# Revit family: Gira_291803
name_source: partatom
category: Electrical Fixtures
revit_build: Autodesk Revit 2017 (Build: 20160225_1515(x64)
units: mm (PartAtom-declared; Revit-internal decimal feet)

## family parameters
Cut with Voids When Loaded = No
Host = Face
Maintain Annotation Orientation = Yes
Part Type = Normal
Room Calculation Point = No
Round Connector Dimension = Use Diameter
Shared = No

## types (1)
- UPS emergency set System 55 p.white
    Assembly arrangement = Basic element
    Available = No
    BIM (1) = https://media.stage.bim.site und Tasten.rfa?public/gira/36a6b08/Sys55_Komplettgerät_Schalten und Tasten.rfa
    Category = System device clinic-installation
    Data sheet (1) = https://katalog.gira.de
    Default Elevation = 1219 mm
    Description = UPS emerg.set Sys55 PW,UPS for the emergency set,,pure white glossy,Features:,- Uninterruptible power supply for the Gira emergency set.,- With drop failure of the mains input voltage, the connected load continues to be supplied via the battery without interruption.,- When the mains input voltage increases again or is applied, the battery is disconnected from the load and recharged in normal mains operation.,- The operating states UPS active" or "Battery defective" can be signalled via the signal contact (M).,,Notes :,- For installations pursuant to DIN 0834.,- DIN 0834 prescribes the replacement of components with limited service lives (battery) once annually.,- Please observe the regulations on the disposal of used batteries."
    GTIN = 4010337011767
    HAN = 291803
    HeinzeBIM = https://bimportal.heinze.de
    Manufacturer = Gira
    Manufacturer URL = https://www.gira.de
    Model = Power adaptor
    Name = UPS emergency set System 55 p.white
    Suitable for bus connection = None
    Type of power supply = External
    URL = http://katalog.gira.de

## geometry (parser evidence)
native form markers: Sweep x12
no freeform markers — native parametric forms only
